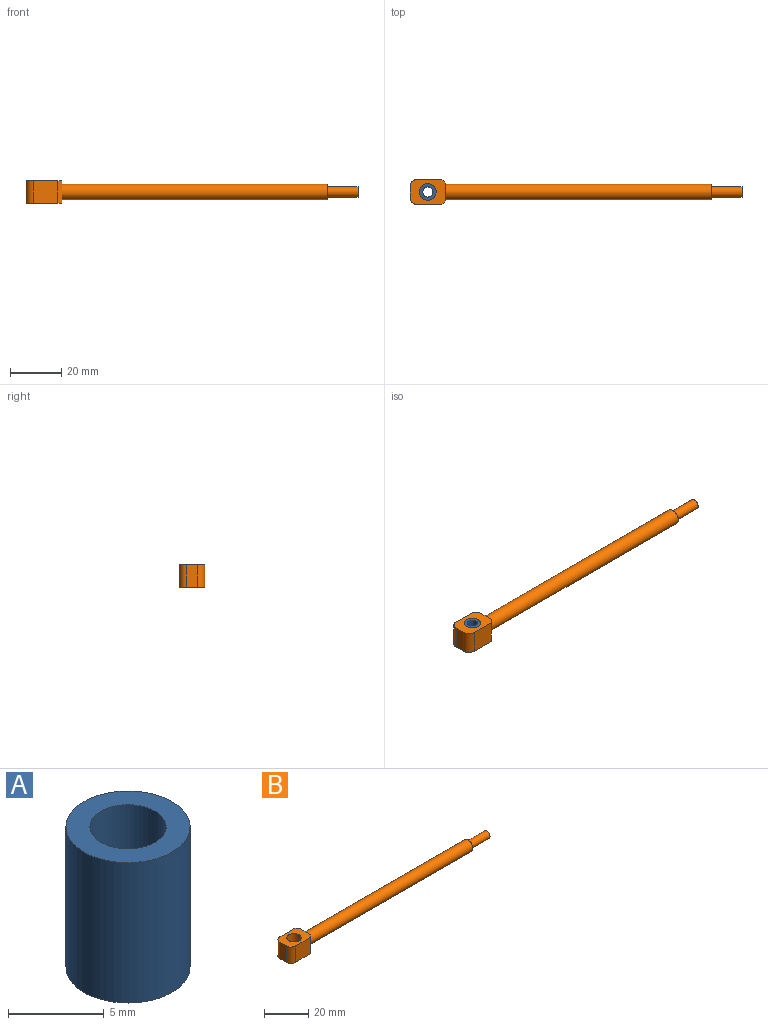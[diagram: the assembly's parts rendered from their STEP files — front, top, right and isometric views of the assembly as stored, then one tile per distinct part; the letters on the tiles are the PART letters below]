
ASSEMBLY  parts=2 mates=1
PART A: 4 faces, bbox 6.5x6.5x9 mm
  f0: cylinder r=2mm len=9mm, axis (0,0,-1), area 113.1mm2, adj f2,f3
  f1: cylinder r=3.25mm len=9mm, axis (0,0,-1), area 183.8mm2, adj f2,f3
  f2: plane 6.5x6.5mm, normal (0,0,1), area 20.6mm2, adj f0,f1
  f3: plane 6.5x6.5mm, normal (0,0,-1), area 20.6mm2, adj f0,f1
PART B: 15 faces, bbox 130x10x9 mm
  f0: cylinder r=3mm len=104mm, axis (-1,0,0), area 1960.4mm2, adj f1,f10
  f1: plane 6x6mm, normal (1,0,0), area 15.7mm2, adj f0,f2
  f2: cylinder r=2mm len=12mm, axis (-1,0,0), area 150.8mm2, adj f1,f3
  f3: plane 4x4mm, normal (1,0,0), area 12.6mm2, adj f2
  f4: plane 9.5x9mm, normal (0,1,0), area 85.5mm2, adj f5,f12,f13,f14
  f5: cylinder r=3mm len=9mm, axis (0,0,-1), area 42.4mm2, adj f4,f6,f13,f14
  f6: plane 9x4mm, normal (-1,0,0), area 36mm2, adj f5,f7,f13,f14
  f7: cylinder r=3mm len=9mm, axis (0,0,-1), area 42.4mm2, adj f6,f8,f13,f14
  f8: plane 9.5x9mm, normal (0,-1,0), area 85.5mm2, adj f7,f9,f13,f14
  f9: plane 9x1.5mm, normal (0.71,-0.71,0), area 19.1mm2, adj f8,f10,f13,f14
  f10: plane 9x7mm, normal (1,0,0), area 34.7mm2, adj f0,f9,f12,f13,f14
  f11: cylinder r=3.25mm len=9mm, axis (0,0,-1), area 183.8mm2, adj f13,f14
  f12: plane 9x1.5mm, normal (0.71,0.71,0), area 19.1mm2, adj f4,f10,f13,f14
  f13: plane 14x10mm, normal (0,0,1), area 100.7mm2, adj f4,f5,f6,f7,f8,f9,f10,f11
  f14: plane 14x10mm, normal (0,0,-1), area 100.7mm2, adj f4,f5,f6,f7,f8,f9,f10,f11
PLACE A t=(66.77,-10.64,-22.52)mm
PLACE B t=(32.17,41.05,-18.02)mm
MATE fastened A.f0 <-> B.f11  axis (0,0,1) through (25.17,41.05,-13.52)mm
